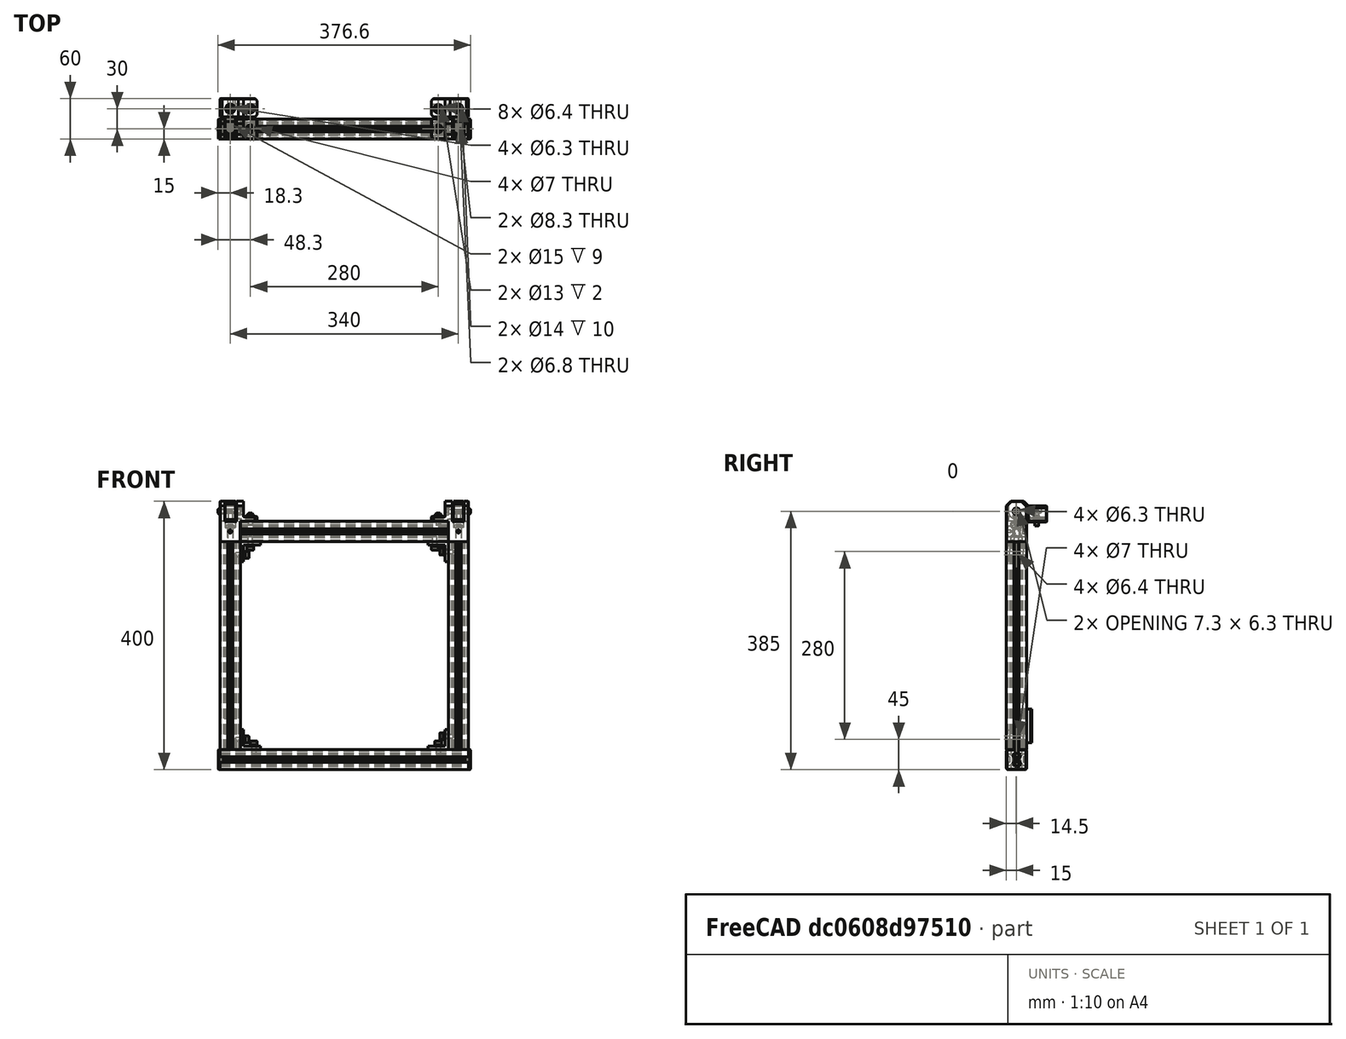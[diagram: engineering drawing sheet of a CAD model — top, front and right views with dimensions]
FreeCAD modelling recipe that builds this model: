
FCSTD DOCUMENT  (FreeCAD 0.19R)
Label: top-lid-assembly
License: Other
LicenseURL: GPL3
objects: Part::FeaturePython×32, Part::Feature×16, PartDesign::CoordinateSystem×1, App::Part×1
note: 49 computed .brp shape members not serialized (recipe doc carries the construction recipe); baked Part::Feature solids carry a one-line shape summary decoded from their .brp

FEATURE [Part::Feature] Extrude002002003001  label="3030-370mm-top-lid-001"
  Placement = pos=(-3e-15,0,15) rot=(0,1,0;1.5708rad)
  shape: bbox 370 x 30 x 30 mm, 95 faces (baked)
FEATURE [Part::Feature] Extrude002002004001  label="3030-310mm-top-lid-001"
  Placement = pos=(15,0,30) rot=(0,0,1;0rad)
  shape: bbox 30 x 30 x 310 mm, 95 faces (baked)
FEATURE [Part::Feature] Extrude002002004002  label="3030-310mm-top-lid-002"
  Placement = pos=(355,0,30) rot=(0,0,1;0rad)
  shape: bbox 30 x 30 x 310 mm, 95 faces (baked)
FEATURE [Part::Feature] Extrude002002004003  label="3030-310mm-top-lid-003"
  Placement = pos=(340,0,355) rot=(0,-1,0;1.5708rad)
  shape: bbox 310 x 30 x 30 mm, 95 faces (baked)
FEATURE [Part::Feature] Chamfer002001010001  label="lid-left-bottom-hinge"
  Placement = pos=(30,45,385) rot=(0,0.707107,-0.707107;3.14159rad)
  shape: bbox 55 x 57 x 31 mm, 55 faces (baked)
FEATURE [Part::Feature] Chamfer002001012001  label="lid-left-top-hinge"
  Placement = pos=(30,15,370) rot=(0,0.707107,-0.707107;3.14159rad)
  shape: bbox 55 x 30 x 65 mm, 86 faces (baked)
FEATURE [Part::Feature] Part__Mirroring003003003005039  label="lid-right-top-hinge"
  Placement = pos=(340,15,370) rot=(0,0.707107,-0.707107;3.14159rad)
  shape: bbox 55 x 30 x 65 mm, 86 faces (baked)
FEATURE [Part::Feature] Part__Mirroring003003003005040  label="lid-right-bottom-hinge"
  Placement = pos=(340,45,385) rot=(0,0.707107,-0.707107;3.14159rad)
  shape: bbox 55 x 57 x 31 mm, 55 faces (baked)
FEATURE [Part::FeaturePython] Screw1392  label="M8x30-Screw"  # Fasteners workbench fastener (typed FeaturePython)
  Placement = pos=(355,1.24e-13,361) rot=(0,0,1;0rad)
  baseObject = -> Part__Mirroring003003003005039 [Edge94]
  diameter = 5
  invert = false
  leftHanded = false
  length = 5
  lengthCustom = 30
  matchOuter = true
  offset = 0
  thread = false
  type = 39
FEATURE [Part::FeaturePython] Screw1393  label="M8x30-Screw001"  # Fasteners workbench fastener (typed FeaturePython)
  Placement = pos=(15,8.2e-14,361) rot=(0,0,1;0rad)
  baseObject = -> Chamfer002001012001 [Edge94]
  diameter = 5
  invert = true
  leftHanded = false
  length = 5
  lengthCustom = 30
  matchOuter = true
  offset = 0
  thread = false
  type = 39
FEATURE [Part::FeaturePython] Washer346  label="M6-Washer156"  # Fasteners workbench fastener (typed FeaturePython)
  Placement = pos=(325,1.23e-13,377) rot=(0,0,1;0rad)
  baseObject = -> Part__Mirroring003003003005039 [Edge130]
  diameter = 2
  invert = true
  matchOuter = true
  offset = 0
  type = 4
FEATURE [Part::FeaturePython] Washer347  label="M6-Washer001"  # Fasteners workbench fastener (typed FeaturePython)
  Placement = pos=(45,8.2e-14,377) rot=(0,0,1;0rad)
  baseObject = -> Chamfer002001012001 [Edge130]
  diameter = 2
  invert = false
  matchOuter = true
  offset = 0
  type = 4
FEATURE [Part::FeaturePython] Screw1394  label="M6x14-Screw"  # Fasteners workbench fastener (typed FeaturePython)
  Placement = pos=(45,8.2e-14,378.8) rot=(0,0,1;0rad)
  baseObject = -> Washer347 [Edge1]
  diameter = 4
  invert = false
  leftHanded = false
  length = 2
  lengthCustom = 14
  matchOuter = true
  offset = 0
  thread = false
  type = 39
FEATURE [Part::FeaturePython] Screw1395  label="M6x14-Screw001"  # Fasteners workbench fastener (typed FeaturePython)
  Placement = pos=(325,1.23e-13,378.8) rot=(0,0,1;0rad)
  baseObject = -> Washer346 [Edge1]
  diameter = 4
  invert = false
  leftHanded = false
  length = 2
  lengthCustom = 14
  matchOuter = true
  offset = 0
  thread = false
  type = 39
FEATURE [Part::FeaturePython] Nut059  label="M6-Nut"  # Fasteners workbench fastener (typed FeaturePython)
  Placement = pos=(30,8.5e-14,385) rot=(0,-1,0;1.5708rad)
  baseObject = -> Chamfer002001012001 [Edge177]
  diameter = 8
  invert = false
  leftHanded = false
  matchOuter = true
  offset = 0
  thread = false
  type = 7
FEATURE [Part::FeaturePython] Nut060  label="M6-Nut001"  # Fasteners workbench fastener (typed FeaturePython)
  Placement = pos=(340,1.28e-13,385) rot=(0,-1,0;1.5708rad)
  baseObject = -> Part__Mirroring003003003005039 [Edge177]
  diameter = 8
  invert = false
  leftHanded = false
  matchOuter = true
  offset = 0
  thread = false
  type = 7
FEATURE [Part::FeaturePython] Screw1396  label="M6x10-Screw120"  # Fasteners workbench fastener (typed FeaturePython)
  Placement = pos=(5e-14,8.5e-14,385) rot=(0,-1,0;1.5708rad)
  baseObject = -> Chamfer002001012001 [Edge70]
  diameter = 4
  invert = false
  leftHanded = false
  length = 0
  lengthCustom = 10
  matchOuter = true
  offset = 0
  thread = false
  type = 39
FEATURE [Part::FeaturePython] Screw1397  label="M6x10-Screw001"  # Fasteners workbench fastener (typed FeaturePython)
  Placement = pos=(370,1.32e-13,385) rot=(0,1,0;1.5708rad)
  baseObject = -> Part__Mirroring003003003005039 [Edge70]
  diameter = 4
  invert = true
  leftHanded = false
  length = 0
  lengthCustom = 10
  matchOuter = true
  offset = 0
  thread = false
  type = 39
FEATURE [Part::FeaturePython] Washer348  label="M6-Washer004"  # Fasteners workbench fastener (typed FeaturePython)
  Placement = pos=(325,30,374) rot=(0,0,1;0rad)
  baseObject = -> Part__Mirroring003003003005040 [Edge130]
  diameter = 7
  invert = false
  matchOuter = true
  offset = 0
  type = 3
FEATURE [Part::FeaturePython] Washer349  label="M6-Washer005"  # Fasteners workbench fastener (typed FeaturePython)
  Placement = pos=(45,30,374) rot=(0,0,1;0rad)
  baseObject = -> Chamfer002001010001 [Edge130]
  diameter = 7
  invert = true
  matchOuter = true
  offset = 0
  type = 3
FEATURE [Part::FeaturePython] Screw1398  label="M6x12-Screw112"  # Fasteners workbench fastener (typed FeaturePython)
  Placement = pos=(325,30,375.8) rot=(0,0,1;0rad)
  baseObject = -> Washer348 [Edge1]
  diameter = 4
  invert = false
  leftHanded = false
  length = 1
  lengthCustom = 12
  matchOuter = true
  offset = 0
  thread = false
  type = 39
FEATURE [Part::FeaturePython] Screw1399  label="M6x12-Screw113"  # Fasteners workbench fastener (typed FeaturePython)
  Placement = pos=(45,30,375.8) rot=(0,0,1;0rad)
  baseObject = -> Washer349 [Edge1]
  diameter = 4
  invert = false
  leftHanded = false
  length = 1
  lengthCustom = 12
  matchOuter = true
  offset = 0
  thread = false
  type = 39
FEATURE [Part::FeaturePython] Screw1400  label="M6x20-Screw"  # Fasteners workbench fastener (typed FeaturePython)
  Placement = pos=(355,30,383) rot=(0,0,1;0rad)
  baseObject = -> Part__Mirroring003003003005040 [Edge133]
  diameter = 4
  invert = false
  leftHanded = false
  length = 4
  lengthCustom = 20
  matchOuter = true
  offset = 0
  thread = false
  type = 39
FEATURE [Part::FeaturePython] Screw1401  label="M6x20-Screw001"  # Fasteners workbench fastener (typed FeaturePython)
  Placement = pos=(15,30,383) rot=(0,0,1;0rad)
  baseObject = -> Chamfer002001010001 [Edge133]
  diameter = 4
  invert = true
  leftHanded = false
  length = 4
  lengthCustom = 20
  matchOuter = true
  offset = 0
  thread = false
  type = 39
FEATURE [Part::Feature] Part__Feature112001142  label="L-corner-bracket028"
  Placement = pos=(340,7.8e-14,340) rot=(0.57735,0.57735,-0.57735;4.18879rad)
  shape: bbox 30 x 20 x 30 mm, 10 faces (baked)
FEATURE [Part::Feature] Part__Feature112001143  label="L-corner-bracket029"
  Placement = pos=(30,7.8e-14,340) rot=(0.707107,0.707107,0;3.14159rad)
  shape: bbox 30 x 20 x 30 mm, 10 faces (baked)
FEATURE [Part::Feature] Part__Feature112001144  label="L-corner-bracket030"
  Placement = pos=(30,7.8e-14,30) rot=(0.57735,0.57735,0.57735;2.0944rad)
  shape: bbox 30 x 20 x 30 mm, 10 faces (baked)
FEATURE [Part::Feature] Part__Feature112001076  label="L-corner-bracket010"
  Placement = pos=(340,7.8e-14,30) rot=(0,0,1;1.5708rad)
  shape: bbox 30 x 20 x 30 mm, 10 faces (baked)
FEATURE [Part::FeaturePython] Washer350  label="M6-Washer006"  # Fasteners workbench fastener (typed FeaturePython)
  Placement = pos=(50,7.4e-14,35) rot=(0,0,1;0rad)
  baseObject = -> Part__Feature112001144 [Edge1]
  diameter = 2
  invert = true
  matchOuter = false
  offset = 0
  type = 4
FEATURE [Part::FeaturePython] Washer351  label="M6-Washer157"  # Fasteners workbench fastener (typed FeaturePython)
  Placement = pos=(35,7.7e-14,45) rot=(0,1,0;1.5708rad)
  baseObject = -> Part__Feature112001144 [Edge7]
  diameter = 2
  invert = true
  matchOuter = false
  offset = 0
  type = 4
FEATURE [Part::FeaturePython] Washer352  label="M6-Washer158"  # Fasteners workbench fastener (typed FeaturePython)
  Placement = pos=(325,7.5e-14,35) rot=(0,0,1;0rad)
  baseObject = -> Part__Feature112001076 [Edge7]
  diameter = 2
  invert = true
  matchOuter = false
  offset = 0
  type = 4
FEATURE [Part::FeaturePython] Washer353  label="M6-Washer159"  # Fasteners workbench fastener (typed FeaturePython)
  Placement = pos=(335,7.7e-14,50) rot=(0,-1,0;1.5708rad)
  baseObject = -> Part__Feature112001076 [Edge4]
  diameter = 2
  invert = true
  matchOuter = false
  offset = 0
  type = 4
FEATURE [Part::FeaturePython] Washer354  label="M6-Washer010"  # Fasteners workbench fastener (typed FeaturePython)
  Placement = pos=(320,7.9e-14,335) rot=(1,0,0;3.14159rad)
  baseObject = -> Part__Feature112001142 [Edge4]
  diameter = 2
  invert = true
  matchOuter = false
  offset = 0
  type = 4
FEATURE [Part::FeaturePython] Washer355  label="M6-Washer011"  # Fasteners workbench fastener (typed FeaturePython)
  Placement = pos=(335,8.1e-14,325) rot=(0,-1,0;1.5708rad)
  baseObject = -> Part__Feature112001142 [Edge7]
  diameter = 2
  invert = true
  matchOuter = false
  offset = 0
  type = 4
FEATURE [Part::FeaturePython] Washer356  label="M6-Washer012"  # Fasteners workbench fastener (typed FeaturePython)
  Placement = pos=(35,7.9e-14,320) rot=(0,1,0;1.5708rad)
  baseObject = -> Part__Feature112001143 [Edge1]
  diameter = 2
  invert = true
  matchOuter = false
  offset = 0
  type = 4
FEATURE [Part::FeaturePython] Washer357  label="M6-Washer013"  # Fasteners workbench fastener (typed FeaturePython)
  Placement = pos=(45,8.1e-14,335) rot=(1,0,0;3.14159rad)
  baseObject = -> Part__Feature112001143 [Edge7]
  diameter = 2
  invert = true
  matchOuter = false
  offset = 0
  type = 4
FEATURE [Part::FeaturePython] Screw1402  label="M6x14-Screw015"  # Fasteners workbench fastener (typed FeaturePython)
  Placement = pos=(325,7.5e-14,36.8) rot=(0,0,1;0rad)
  baseObject = -> Washer352 [Edge1]
  diameter = 7
  invert = false
  leftHanded = false
  length = 3
  lengthCustom = 14
  matchOuter = false
  offset = 0
  thread = false
  type = 33
FEATURE [Part::FeaturePython] Screw1403  label="M6x14-Screw016"  # Fasteners workbench fastener (typed FeaturePython)
  Placement = pos=(333.2,7.7e-14,50) rot=(0,-1,0;1.5708rad)
  baseObject = -> Washer353 [Edge1]
  diameter = 7
  invert = false
  leftHanded = false
  length = 3
  lengthCustom = 14
  matchOuter = false
  offset = 0
  thread = false
  type = 33
FEATURE [Part::FeaturePython] Screw1404  label="M6x14-Screw013"  # Fasteners workbench fastener (typed FeaturePython)
  Placement = pos=(36.8,7.7e-14,45) rot=(0,1,0;1.5708rad)
  baseObject = -> Washer351 [Edge1]
  diameter = 7
  invert = false
  leftHanded = false
  length = 3
  lengthCustom = 14
  matchOuter = false
  offset = 0
  thread = false
  type = 33
FEATURE [Part::FeaturePython] Screw1405  label="M6x14-Screw014"  # Fasteners workbench fastener (typed FeaturePython)
  Placement = pos=(50,7.4e-14,36.8) rot=(0,0,1;0rad)
  baseObject = -> Washer350 [Edge1]
  diameter = 7
  invert = false
  leftHanded = false
  length = 3
  lengthCustom = 14
  matchOuter = false
  offset = 0
  thread = false
  type = 33
FEATURE [Part::FeaturePython] Screw016  label="M6x14-Screw011"  # Fasteners workbench fastener (typed FeaturePython)
  Placement = pos=(36.8,7.9e-14,320) rot=(0,1,0;1.5708rad)
  baseObject = -> Washer356 [Edge1]
  diameter = 7
  invert = false
  leftHanded = false
  length = 3
  lengthCustom = 14
  matchOuter = false
  offset = 0
  thread = false
  type = 33
FEATURE [Part::FeaturePython] Screw1406  label="M6x14-Screw012"  # Fasteners workbench fastener (typed FeaturePython)
  Placement = pos=(45,8.1e-14,333.2) rot=(1,0,0;3.14159rad)
  baseObject = -> Washer357 [Edge1]
  diameter = 7
  invert = false
  leftHanded = false
  length = 3
  lengthCustom = 14
  matchOuter = false
  offset = 0
  thread = false
  type = 33
FEATURE [Part::FeaturePython] Screw1407  label="M6x14-Screw010"  # Fasteners workbench fastener (typed FeaturePython)
  Placement = pos=(320,7.9e-14,333.2) rot=(1,0,0;3.14159rad)
  baseObject = -> Washer354 [Edge1]
  diameter = 7
  invert = false
  leftHanded = false
  length = 3
  lengthCustom = 14
  matchOuter = false
  offset = 0
  thread = false
  type = 33
FEATURE [Part::FeaturePython] Screw1408  label="M6x14-Screw009"  # Fasteners workbench fastener (typed FeaturePython)
  Placement = pos=(333.2,8.1e-14,325) rot=(0,-1,0;1.5708rad)
  baseObject = -> Washer355 [Edge1]
  diameter = 7
  invert = false
  leftHanded = false
  length = 3
  lengthCustom = 14
  matchOuter = false
  offset = 0
  thread = false
  type = 33
FEATURE [Part::Feature] Chamfer002001018001001001
  Placement = pos=(15,15,90) rot=(1,0,0;3.14159rad)
  shape: bbox 16 x 16 x 60 mm, 19 faces (baked)
FEATURE [Part::Feature] Chamfer002001018001001002
  Placement = pos=(355,15,90) rot=(1,0,0;3.14159rad)
  shape: bbox 16 x 16 x 60 mm, 19 faces (baked)
FEATURE [Part::Feature] Fusion003012003006001  label="lid-end-cap001"
  Placement = pos=(-3e-15,0,15) rot=(0.707107,0,0.707107;3.14159rad)
  shape: bbox 10 x 30 x 30 mm, 385 faces (baked)
FEATURE [Part::Feature] Fusion003012003006002  label="lid-end-cap002"
  Placement = pos=(370,0,15) rot=(0.707107,0,-0.707107;3.14159rad)
  shape: bbox 10 x 30 x 30 mm, 385 faces (baked)
FEATURE [PartDesign::CoordinateSystem] LCS_top_lid  label="LCS_top-lid"
  AttacherType = Attacher::AttachEngine3D
  AttachmentOffset = pos=(-15,0,0) rot=(0,0,1;0rad)
  MapMode = 45
  Placement = pos=(185,15,-8.9) rot=(0.57735,0.57735,0.57735;4.18879rad)
  Support = -> [Extrude002002003001]
FEATURE [App::Part] Part199  label="top-lid"
  Group = -> [Extrude002002003001,Extrude002002004001,Extrude002002004002,Extrude002002004003,Washer349,Screw1399,Screw1401,Chamfer002001010001,Screw1393,Washer347,Screw1394,Nut059,Screw1396,Chamfer002001012001,Screw1392,Washer346,Screw1395,Nut060,Screw1397,Part__Mirroring003003003005039,Washer348,Screw1398,Screw1400,Part__Mirroring003003003005040,Washer355,Washer354,Screw1408,Screw1407,Part__Feature112001142,+20 more]
  Origin = -> Origin208
  Placement = pos=(0,5.79e-14,0) rot=(-1,0,0;1.5708rad)
